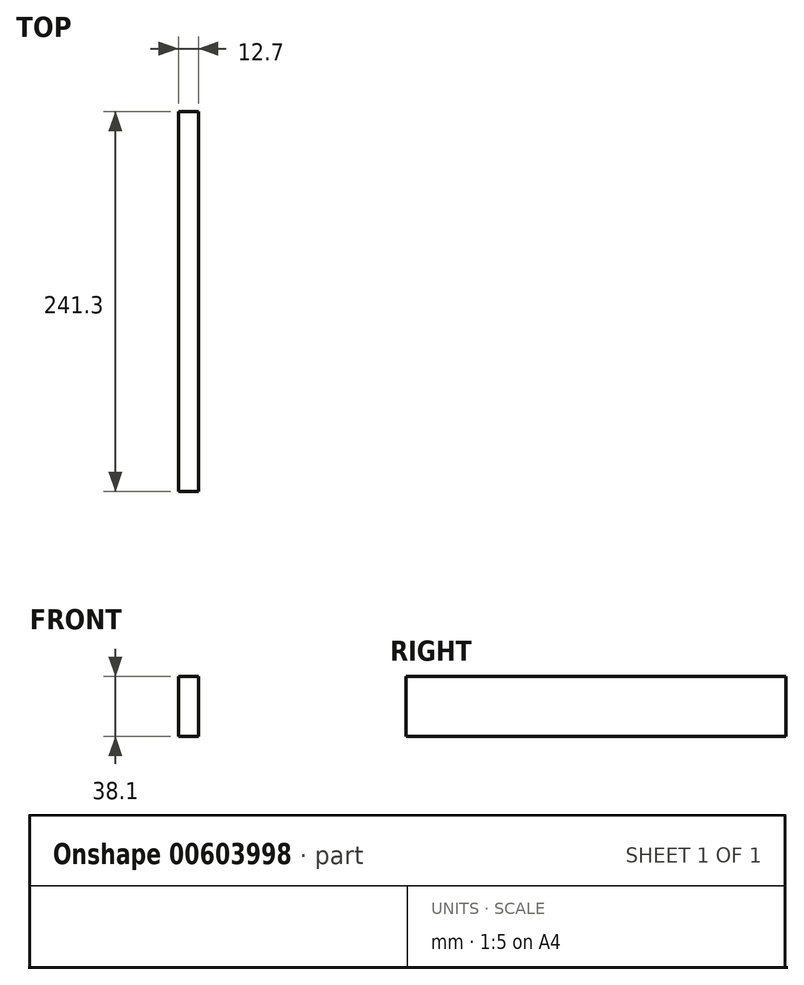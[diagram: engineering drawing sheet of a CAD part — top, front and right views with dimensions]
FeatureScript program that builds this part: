
annotation { "Feature Type Name" : "Feature", "Feature Type Description" : "" }
export const myFeature = defineFeature(function(context is Context, id is Id, definition is map)
    precondition{}
    {
        {
            var Q0;
            Q0=qCreatedBy(makeId("Front.planeOp"),FACE);
            var sketch = newSketch(context, id + "F0", { "sketchPlane" : qUnion([Q0])});
            skLineSegment(sketch, "E0.bottom", {"start": v(0, 0) * mm, "end": v(12.7, 0) * mm});
            skLineSegment(sketch, "E0.top", {"start": v(0, 38.1) * mm, "end": v(12.7, 38.1) * mm});
            skLineSegment(sketch, "E0.left", {"start": v(0, 0) * mm, "end": v(0, 38.1) * mm});
            skLineSegment(sketch, "E0.right", {"start": v(12.7, 0) * mm, "end": v(12.7, 38.1) * mm});
            skSolve(sketch);
        }
        {
            var Q0;
            Q0=makeQuery(id+"F0.imprint","IMPRINT",FACE,{"disambiguationData":[TD([[makeQuery(id+"F0.imprint","IMPRINT",EDGE,{"derivedFrom":sQuery(id+"F0.wireOp",EDGE,"E0.bottom")}),1.0]])]});
            extrude(context, id + "F1", {"entities" : qUnion([Q0]), "depth" : 241.3 * mm, "offsetDistance" : 25.4 * mm});
        }
    });
